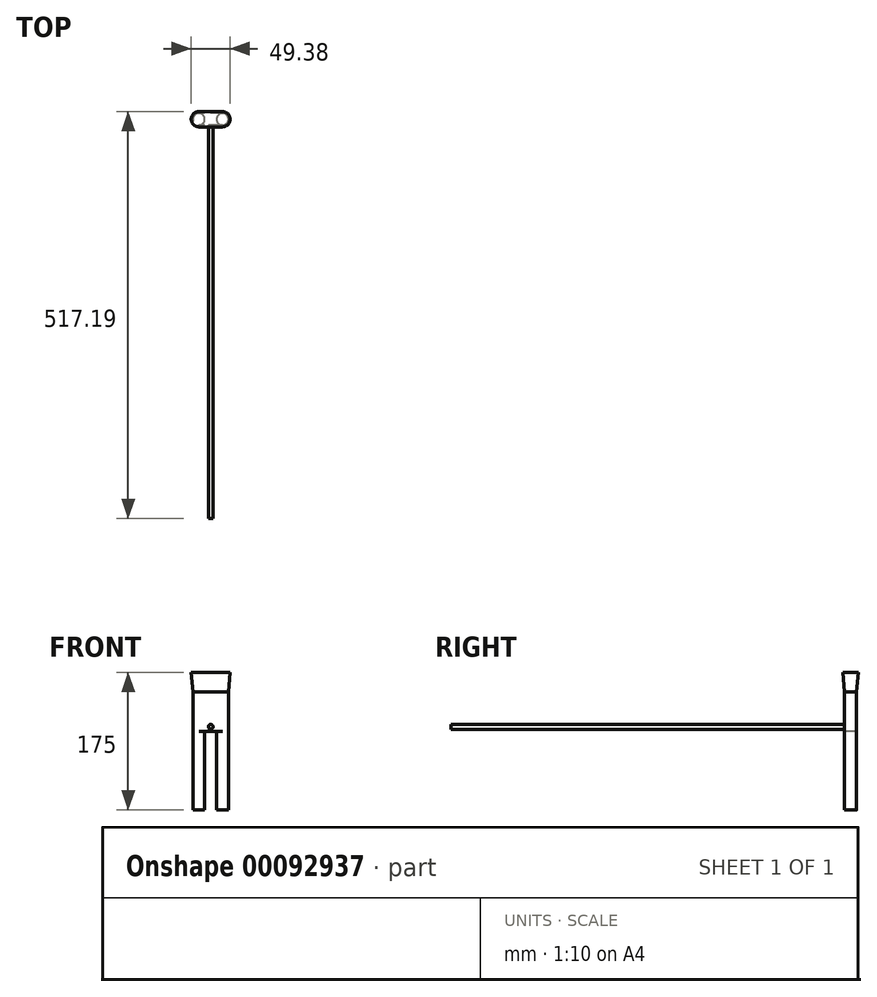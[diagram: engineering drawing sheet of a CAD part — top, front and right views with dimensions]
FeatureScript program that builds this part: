
annotation { "Feature Type Name" : "Feature", "Feature Type Description" : "" }
export const myFeature = defineFeature(function(context is Context, id is Id, definition is map)
    precondition{}
    {
        {
            var Q0;
            Q0=qCreatedBy(makeId("Top.planeOp"),FACE);
            var sketch = newSketch(context, id + "F0", { "sketchPlane" : qUnion([Q0])});
            skLineSegment(sketch, "E0.bottom", {"start": v(15, 7.5) * mm, "end": v(-15, 7.5) * mm});
            skLineSegment(sketch, "E0.top", {"start": v(15, -7.5) * mm, "end": v(-15, -7.5) * mm});
            skPoint(sketch, "E0.middle", {"position": v(0, 0) * mm});
            skArc(sketch, "E1", {"start": v(15, -7.5) * mm, "mid": v(22.5, 0) * mm, "end": v(15, 7.5) * mm});
            skArc(sketch, "E2", {"start": v(-15, 7.5) * mm, "mid": v(-22.5, 0) * mm, "end": v(-15, -7.5) * mm});
            skSolve(sketch);
        }
        {
            var Q0;
            Q0 = qSketchRegion(id + "F0", true);
            extrude(context, id + "F1", {"entities" : qUnion([Q0]), "depth" : 50 * mm});
        }
        {
            var Q0;
            Q0=makeQuery(id+"F1.opExtrude","SWEPT_FACE",FACE,{"disambiguationData":[OSD([sQuery(id+"F0.wireOp",EDGE,"E0.top")])]});
            var sketch = newSketch(context, id + "F2", { "sketchPlane" : qUnion([Q0])});
            skCircle(sketch, "E3", {"center": v(0, 18.25) * mm, "radius": 1 * mm});
            skSolve(sketch);
        }
        {
            var Q0;
            Q0=makeQuery(id+"F1.opExtrude","CAP_FACE",FACE,{"disambiguationData":[OSD([sQuery(id+"F0.wireOp",EDGE,"E0.bottom"),sQuery(id+"F0.wireOp",EDGE,"E0.top"),sQuery(id+"F0.wireOp",EDGE,"E1"),sQuery(id+"F0.wireOp",EDGE,"E2")])],"isStart":true});
            var sketch = newSketch(context, id + "F3", { "sketchPlane" : qUnion([Q0])});
            skCircle(sketch, "E4", {"center": v(-15, 0) * mm, "radius": 7.5 * mm});
            skCircle(sketch, "E5", {"center": v(15, 0) * mm, "radius": 7.5 * mm});
            skSolve(sketch);
        }
        {
            var Q0;
            Q0 = qSketchRegion(id + "F3", true);
            extrude(context, id + "F4", {"entities" : qUnion([Q0]), "operationType" : NewBodyOperationType.ADD, "depth" : 100 * mm});
        }
        {
            var Q0;
            Q0=makeQuery(id+"F2.imprint","IMPRINT",FACE,{"disambiguationData":[TD([[makeQuery(id+"F2.imprint","IMPRINT",EDGE,{"derivedFrom":sQuery(id+"F2.wireOp",EDGE,"E3")}),-1.0]])]});
            var sketch = newSketch(context, id + "F5", { "sketchPlane" : qUnion([Q0])});
            skCircle(sketch, "E6", {"center": v(0, 5.64) * mm, "radius": 3 * mm});
            skSolve(sketch);
        }
        {
            var Q0;
            Q0 = qSketchRegion(id + "F5", true);
            extrude(context, id + "F6", {"entities" : qUnion([Q0]), "operationType" : NewBodyOperationType.ADD, "depth" : 500 * mm});
        }
        {
            var Q0;
            Q0=makeQuery(id+"F1.opExtrude","CAP_FACE",FACE,{"disambiguationData":[OSD([sQuery(id+"F0.wireOp",EDGE,"E0.bottom"),sQuery(id+"F0.wireOp",EDGE,"E0.top"),sQuery(id+"F0.wireOp",EDGE,"E1"),sQuery(id+"F0.wireOp",EDGE,"E2")])],"isStart":false});
            var sketch = newSketch(context, id + "F7", { "sketchPlane" : qUnion([Q0])});
            skCircle(sketch, "E7", {"center": v(15, 0) * mm, "radius": 7.5 * mm});
            skCircle(sketch, "E8", {"center": v(-15, 0) * mm, "radius": 7.5 * mm});
            skLineSegment(sketch, "E9.bottom", {"start": v(-15, -7.5) * mm, "end": v(15, -7.5) * mm});
            skLineSegment(sketch, "E9.top", {"start": v(-15, 7.5) * mm, "end": v(15, 7.5) * mm});
            skLineSegment(sketch, "E9.left", {"start": v(-15, -7.5) * mm, "end": v(-15, 7.5) * mm});
            skLineSegment(sketch, "E9.right", {"start": v(15, -7.5) * mm, "end": v(15, 7.5) * mm});
            skSolve(sketch);
        }
        {
            var Q0;
            Q0 = qSketchRegion(id + "F7", true);
            extrude(context, id + "F8", {"entities" : qUnion([Q0]), "operationType" : NewBodyOperationType.ADD, "depth" : 25 * mm, "hasDraft" : true, "draftAngle" : 5 * degree});
        }
    });
